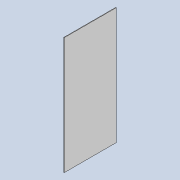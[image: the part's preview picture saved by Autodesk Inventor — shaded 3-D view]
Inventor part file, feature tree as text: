
AUTODESK INVENTOR PART (.ipt)
format: ipt  version: 2022 (Build 260153000, 153)  size: 97,280 bytes
history: native  units: in
note: dims shown in document units (in); Inventor stores cm internally (conversion verified against a paired STEP export)
features: extrude x2, sketch x2, projected_geometry x1
ambient origin geometry x8: Origin, YZ Plane, XZ Plane, XY Plane, X Axis, Y Axis, Z Axis, Center Point
bodies: Solid1 (feature_tree)
feature tree (5):
  extrude  "Extrusion1"  Depth=22.0in
  extrude  "Extrusion2"  Depth=0.125in
  sketch  "Sketch1"  dims[d0=51.0in d1=22.0in]
  sketch  "Sketch2"  dims[d2=0.125in d3=0.0in d4=0.17in d5=0.5in d6=0.5in d7=0.17in d8=0.5in d9=0.5in d10=0.17in d11=0.17in d12=0.5in d13=0.5in d14=0.5in d15=0.5in d16=0.125in d17=0.0in]
  projected_geometry  "Projected Loop1"
